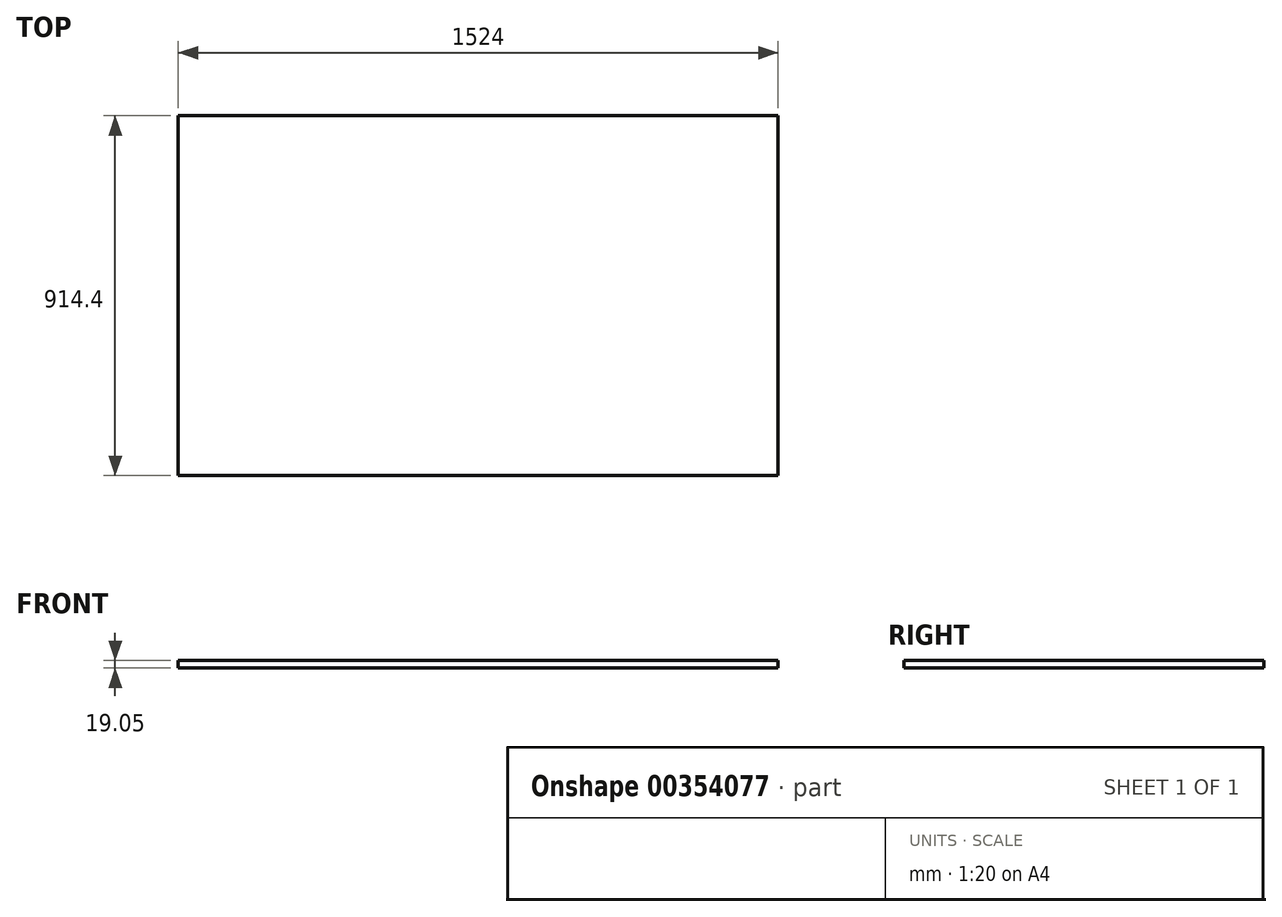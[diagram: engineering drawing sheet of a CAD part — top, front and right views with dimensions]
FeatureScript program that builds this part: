
annotation { "Feature Type Name" : "Feature", "Feature Type Description" : "" }
export const myFeature = defineFeature(function(context is Context, id is Id, definition is map)
    precondition{}
    {
        {
            var Q0;
            Q0=qCreatedBy(makeId("Top.planeOp"),FACE);
            var sketch = newSketch(context, id + "F0", { "sketchPlane" : qUnion([Q0])});
            skLineSegment(sketch, "E0.bottom", {"start": v(-762.13, 492.2) * mm, "end": v(761.87, 492.2) * mm});
            skLineSegment(sketch, "E0.top", {"start": v(-762.13, -422.2) * mm, "end": v(761.87, -422.2) * mm});
            skLineSegment(sketch, "E0.left", {"start": v(-762.13, 492.2) * mm, "end": v(-762.13, -422.2) * mm});
            skLineSegment(sketch, "E0.right", {"start": v(761.87, 492.2) * mm, "end": v(761.87, -422.2) * mm});
            skSolve(sketch);
        }
        {
            var Q0;
            Q0 = qSketchRegion(id + "F0", true);
            extrude(context, id + "F1", {"entities" : qUnion([Q0]), "depth" : 19.05 * mm});
        }
    });
